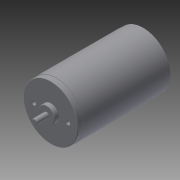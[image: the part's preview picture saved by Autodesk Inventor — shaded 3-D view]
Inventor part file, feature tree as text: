
AUTODESK INVENTOR PART (.ipt)
format: ipt  version: 2014 (Build 180170000, 170)  size: 133,120 bytes
history: native  units: in
note: dims shown in document units (in); Inventor stores cm internally (conversion verified against a paired STEP export)
features: chamfer x1, other x1, imported_body x1
ambient origin geometry x8: Origin, YZ Plane, XZ Plane, XY Plane, X Axis, Y Axis, Z Axis, Center Point
bodies: Body1 (feature_tree)
feature tree (3):
  chamfer  "Chamfer1"  [1 undecoded]
  other  "217-3351-STEP1"
  imported_body  "Base1"
note: 1 required parameter value undecoded (feature->parameter linkage not recoverable at this tier; creation-order binding heuristic only, values carry confidence <= 0.55)
